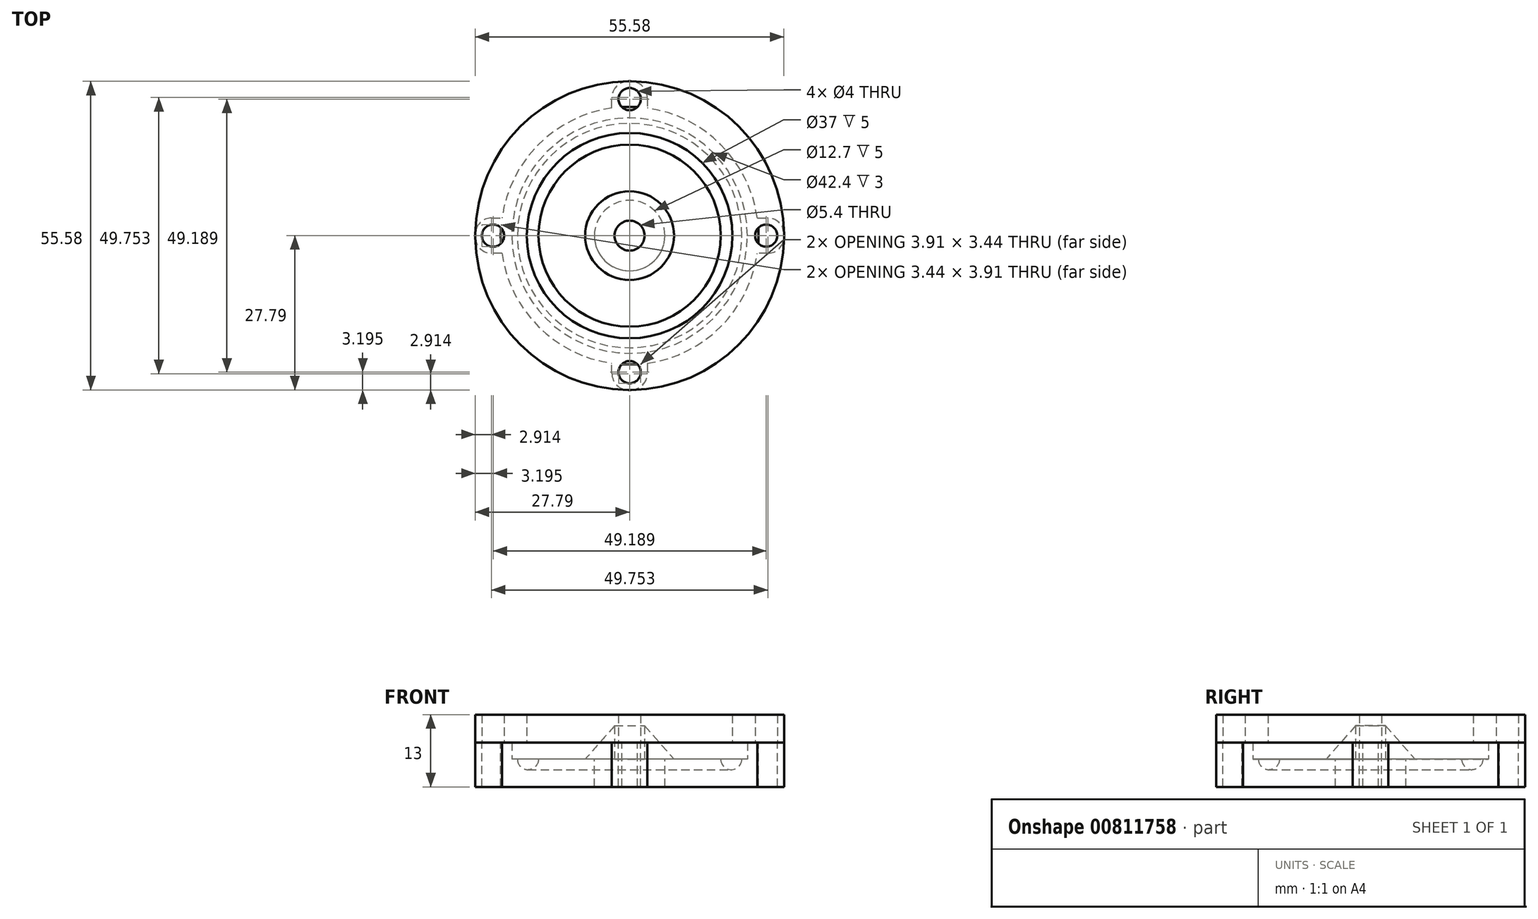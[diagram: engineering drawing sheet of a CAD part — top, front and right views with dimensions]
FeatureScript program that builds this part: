
annotation { "Feature Type Name" : "Feature", "Feature Type Description" : "" }
export const myFeature = defineFeature(function(context is Context, id is Id, definition is map)
    precondition{}
    {
        {
            assignVariable(context, id + "F0", {"name" : "thickness", "anyValue" : 5});
        }
        {
            var Q0;
            Q0=qCreatedBy(makeId("Top.planeOp"),FACE);
            var sketch = newSketch(context, id + "F1", { "sketchPlane" : qUnion([Q0])});
            skCircle(sketch, "E0", {"center": v(0, 0) * mm, "radius": 23.2 * mm});
            skCircle(sketch, "E1", {"center": v(0, 0) * mm, "radius": 21.2 * mm});
            skCircle(sketch, "E2", {"center": v(0, 0) * mm, "radius": 6.35 * mm});
            skSolve(sketch);
        }
        {
            var Q0;
            Q0=makeQuery(id+"F1.imprint","IMPRINT",FACE,{"disambiguationData":[TD([[makeQuery(id+"F1.imprint","IMPRINT",EDGE,{"derivedFrom":sQuery(id+"F1.wireOp",EDGE,"E1")}),1.0]])]});
            var Q1;
            Q1=makeQuery(id+"F1.imprint","IMPRINT",FACE,{"disambiguationData":[TD([[makeQuery(id+"F1.imprint","IMPRINT",EDGE,{"derivedFrom":sQuery(id+"F1.wireOp",EDGE,"E0")}),1.0]])]});
            extrude(context, id + "F2", {"entities" : qUnion([Q0, Q1]), "oppositeDirection" : true, "depth" : getVariable(context, 'thickness') * mm, "offsetDistance" : 25 * mm});
        }
        {
            var Q0;
            Q0=makeQuery(id+"F1.imprint","IMPRINT",FACE,{"disambiguationData":[TD([[makeQuery(id+"F1.imprint","IMPRINT",EDGE,{"derivedFrom":sQuery(id+"F1.wireOp",EDGE,"E0")}),1.0]])]});
            extrude(context, id + "F3", {"entities" : qUnion([Q0]), "operationType" : NewBodyOperationType.ADD, "depth" : 3 * mm, "offsetDistance" : 25 * mm});
        }
        {
            var Q0;
            Q0=qCreatedBy(makeId("Front.planeOp"),FACE);
            var sketch = newSketch(context, id + "F4", { "sketchPlane" : qUnion([Q0])});
            skLineSegment(sketch, "E3.0", {"start": v(-21.2, 0) * mm, "end": v(21.2, 0) * mm, "construction": true});
            skLineSegment(sketch, "E4", {"start": v(20.2, 0) * mm, "end": v(16.4, 0) * mm});
            skArc(sketch, "E5", {"start": v(16.4, 0) * mm, "mid": v(18.3, -1.9) * mm, "end": v(20.2, 0) * mm});
            skSolve(sketch);
        }
        {
            var Q0;
            Q0=makeQuery(id+"F4.imprint","IMPRINT",FACE,{"disambiguationData":[TD([[makeQuery(id+"F4.imprint","IMPRINT",EDGE,{"derivedFrom":sQuery(id+"F4.wireOp",EDGE,"E4")}),1.0]])]});
            var Q1;
            Q1=sQuery(id+"F1.wireOp",EDGE,"E1");
            revolve(context, id + "F5", {"operationType" : NewBodyOperationType.REMOVE, "surfaceOperationType" : NewSurfaceOperationType.NEW, "entities" : qUnion([Q0]), "axis" : qUnion([Q1]), "revolveType" : RevolveType.FULL, "oppositeDirection" : true});
        }
        {
            var Q0;
            Q0=makeQuery(id+"F3.opExtrude","CAP_FACE",FACE,{"disambiguationData":[OSD([sQuery(id+"F1.wireOp",EDGE,"E0"),sQuery(id+"F1.wireOp",EDGE,"E1")])],"isStart":false});
            var sketch = newSketch(context, id + "F6", { "sketchPlane" : qUnion([Q0])});
            skCircle(sketch, "E6.0", {"center": v(0, 0) * mm, "radius": 23.2 * mm, "construction": true});
            skLineSegment(sketch, "E7", {"start": v(-22.98, 3.2) * mm, "end": v(-24.8, 3.2) * mm});
            skLineSegment(sketch, "E8", {"start": v(-27.8, 0.2) * mm, "end": v(-27.8, -0.2) * mm});
            skLineSegment(sketch, "E9", {"start": v(-24.8, -3.2) * mm, "end": v(-22.98, -3.2) * mm});
            skLineSegment(sketch, "E10", {"start": v(0, 0) * mm, "end": v(-60.22, 0) * mm, "construction": true});
            skPoint(sketch, "E11", {"position": v(-27.8, 0) * mm});
            skCircle(sketch, "E12", {"center": v(-24.6, 0) * mm, "radius": 2 * mm});
            skPoint(sketch, "E13.visualSharp", {"position": v(-27.8, 3.2) * mm});
            skArc(sketch, "E13.filletArc", {"start": v(-24.8, 3.2) * mm, "mid": v(-26.92, 2.32) * mm, "end": v(-27.8, 0.2) * mm});
            skPoint(sketch, "E14.visualSharp", {"position": v(-27.8, -3.2) * mm});
            skArc(sketch, "E14.filletArc", {"start": v(-27.8, -0.2) * mm, "mid": v(-26.92, -2.32) * mm, "end": v(-24.8, -3.2) * mm});
            skPoint(sketch, "E15.1.0", {"position": v(3.2, -27.8) * mm});
            skPoint(sketch, "E15.1.1", {"position": v(0, -27.8) * mm});
            skArc(sketch, "E15.1.2", {"start": v(0.2, -27.8) * mm, "mid": v(2.32, -26.92) * mm, "end": v(3.2, -24.8) * mm});
            skLineSegment(sketch, "E15.1.3", {"start": v(-0.2, -27.8) * mm, "end": v(0.2, -27.8) * mm});
            skArc(sketch, "E15.1.4", {"start": v(-3.2, -24.8) * mm, "mid": v(-2.32, -26.92) * mm, "end": v(-0.2, -27.8) * mm});
            skPoint(sketch, "E15.1.5", {"position": v(-3.2, -27.8) * mm});
            skLineSegment(sketch, "E15.1.6", {"start": v(3.2, -24.8) * mm, "end": v(3.2, -22.98) * mm});
            skCircle(sketch, "E15.1.7", {"center": v(0, -24.6) * mm, "radius": 2 * mm});
            skLineSegment(sketch, "E15.1.8", {"start": v(-3.2, -22.98) * mm, "end": v(-3.2, -24.8) * mm});
            skPoint(sketch, "E15.2.0", {"position": v(27.8, 3.2) * mm});
            skPoint(sketch, "E15.2.1", {"position": v(27.8, 0) * mm});
            skArc(sketch, "E15.2.2", {"start": v(27.8, 0.2) * mm, "mid": v(26.92, 2.32) * mm, "end": v(24.8, 3.2) * mm});
            skLineSegment(sketch, "E15.2.3", {"start": v(27.8, -0.2) * mm, "end": v(27.8, 0.2) * mm});
            skArc(sketch, "E15.2.4", {"start": v(24.8, -3.2) * mm, "mid": v(26.92, -2.32) * mm, "end": v(27.8, -0.2) * mm});
            skPoint(sketch, "E15.2.5", {"position": v(27.8, -3.2) * mm});
            skLineSegment(sketch, "E15.2.6", {"start": v(24.8, 3.2) * mm, "end": v(22.98, 3.2) * mm});
            skCircle(sketch, "E15.2.7", {"center": v(24.6, 0) * mm, "radius": 2 * mm});
            skLineSegment(sketch, "E15.2.8", {"start": v(22.98, -3.2) * mm, "end": v(24.8, -3.2) * mm});
            skPoint(sketch, "E15.3.0", {"position": v(-3.2, 27.8) * mm});
            skPoint(sketch, "E15.3.1", {"position": v(0, 27.8) * mm});
            skArc(sketch, "E15.3.2", {"start": v(-0.2, 27.8) * mm, "mid": v(-2.32, 26.92) * mm, "end": v(-3.2, 24.8) * mm});
            skLineSegment(sketch, "E15.3.3", {"start": v(0.2, 27.8) * mm, "end": v(-0.2, 27.8) * mm});
            skArc(sketch, "E15.3.4", {"start": v(3.2, 24.8) * mm, "mid": v(2.32, 26.92) * mm, "end": v(0.2, 27.8) * mm});
            skPoint(sketch, "E15.3.5", {"position": v(3.2, 27.8) * mm});
            skLineSegment(sketch, "E15.3.6", {"start": v(-3.2, 24.8) * mm, "end": v(-3.2, 22.98) * mm});
            skCircle(sketch, "E15.3.7", {"center": v(0, 24.6) * mm, "radius": 2 * mm});
            skLineSegment(sketch, "E15.3.8", {"start": v(3.2, 22.98) * mm, "end": v(3.2, 24.8) * mm});
            skSolve(sketch);
        }
        {
            var Q0;
            {var subQ1=sQuery(id+"F6.wireOp",EDGE,"E7");Q0=makeQuery(id+"F6.imprint","IMPRINT",FACE,{"disambiguationData":[TD([[makeQuery(id+"F6.imprint","IMPRINT",EDGE,{"derivedFrom":subQ1}),1.0]])]});}
            var Q1;
            Q1=makeQuery(id+"F6.imprint","IMPRINT",FACE,{"disambiguationData":[TD([[makeQuery(id+"F6.imprint","IMPRINT",EDGE,{"derivedFrom":sQuery(id+"F6.wireOp",EDGE,"E15.3.2")}),1.0]])]});
            var Q2;
            Q2=makeQuery(id+"F6.imprint","IMPRINT",FACE,{"disambiguationData":[TD([[makeQuery(id+"F6.imprint","IMPRINT",EDGE,{"derivedFrom":sQuery(id+"F6.wireOp",EDGE,"E15.2.2")}),1.0]])]});
            var Q3;
            Q3=makeQuery(id+"F6.imprint","IMPRINT",FACE,{"disambiguationData":[TD([[makeQuery(id+"F6.imprint","IMPRINT",EDGE,{"derivedFrom":sQuery(id+"F6.wireOp",EDGE,"E15.1.2")}),1.0]])]});
            var Q4;
            Q4=makeQuery(id+"F2.opExtrude","CAP_FACE",FACE,{"disambiguationData":[OSD([sQuery(id+"F1.wireOp",EDGE,"E0")])],"isStart":false});
            extrude(context, id + "F7", {"entities" : qUnion([Q0, Q1, Q2, Q3]), "operationType" : NewBodyOperationType.ADD, "endBound" : BoundingType.UP_TO_SURFACE, "oppositeDirection" : true, "depth" : 25 * mm, "endBoundEntityFace" : qUnion([Q4]), "offsetDistance" : 25 * mm});
        }
        {
            var Q0;
            {var subQ0=sQuery(id+"F1.wireOp",EDGE,"E0");Q0=makeQuery(id+"F7.boolean.opBoolean","MERGE",FACE,{"derivedFrom":[makeQuery(id+"F3.opExtrude","CAP_FACE",FACE,{"disambiguationData":[OSD([subQ0,sQuery(id+"F1.wireOp",EDGE,"E1")])],"isStart":false}),makeQuery(id+"F7.opExtrude","CAP_FACE",FACE,{"disambiguationData":[OSD([subQ0,sQuery(id+"F6.wireOp",EDGE,"E7"),sQuery(id+"F6.wireOp",EDGE,"E8"),sQuery(id+"F6.wireOp",EDGE,"E9"),sQuery(id+"F6.wireOp",EDGE,"E12"),sQuery(id+"F6.wireOp",EDGE,"E13.filletArc"),sQuery(id+"F6.wireOp",EDGE,"E14.filletArc")])],"isStart":true}),makeQuery(id+"F7.opExtrude","CAP_FACE",FACE,{"disambiguationData":[OSD([subQ0,sQuery(id+"F6.wireOp",EDGE,"E15.1.2"),sQuery(id+"F6.wireOp",EDGE,"E15.1.3"),sQuery(id+"F6.wireOp",EDGE,"E15.1.4"),sQuery(id+"F6.wireOp",EDGE,"E15.1.6"),sQuery(id+"F6.wireOp",EDGE,"E15.1.7"),sQuery(id+"F6.wireOp",EDGE,"E15.1.8")])],"isStart":true}),makeQuery(id+"F7.opExtrude","CAP_FACE",FACE,{"disambiguationData":[OSD([subQ0,sQuery(id+"F6.wireOp",EDGE,"E15.2.2"),sQuery(id+"F6.wireOp",EDGE,"E15.2.3"),sQuery(id+"F6.wireOp",EDGE,"E15.2.4"),sQuery(id+"F6.wireOp",EDGE,"E15.2.6"),sQuery(id+"F6.wireOp",EDGE,"E15.2.7"),sQuery(id+"F6.wireOp",EDGE,"E15.2.8")])],"isStart":true}),makeQuery(id+"F7.opExtrude","CAP_FACE",FACE,{"disambiguationData":[OSD([subQ0,sQuery(id+"F6.wireOp",EDGE,"E15.3.2"),sQuery(id+"F6.wireOp",EDGE,"E15.3.3"),sQuery(id+"F6.wireOp",EDGE,"E15.3.4"),sQuery(id+"F6.wireOp",EDGE,"E15.3.6"),sQuery(id+"F6.wireOp",EDGE,"E15.3.7"),sQuery(id+"F6.wireOp",EDGE,"E15.3.8")])],"isStart":true})]});}
            var sketch = newSketch(context, id + "F8", { "sketchPlane" : qUnion([Q0])});
            skArc(sketch, "E16.0", {"start": v(-3.2, 22.98) * mm, "mid": v(-16.4, 16.4) * mm, "end": v(-22.98, 3.2) * mm});
            skArc(sketch, "E16.1", {"start": v(22.98, 3.2) * mm, "mid": v(16.4, 16.4) * mm, "end": v(3.2, 22.98) * mm});
            skArc(sketch, "E16.2", {"start": v(3.2, -22.98) * mm, "mid": v(16.4, -16.4) * mm, "end": v(22.98, -3.2) * mm});
            skArc(sketch, "E16.3", {"start": v(-22.98, -3.2) * mm, "mid": v(-16.4, -16.4) * mm, "end": v(-3.2, -22.98) * mm});
            skLineSegment(sketch, "E16.4", {"start": v(-24.8, -3.2) * mm, "end": v(-22.98, -3.2) * mm});
            skArc(sketch, "E16.5", {"start": v(-27.8, -0.2) * mm, "mid": v(-26.92, -2.32) * mm, "end": v(-24.8, -3.2) * mm});
            skLineSegment(sketch, "E16.6", {"start": v(-27.8, 0.2) * mm, "end": v(-27.8, -0.2) * mm});
            skArc(sketch, "E16.7", {"start": v(-24.8, 3.2) * mm, "mid": v(-26.92, 2.32) * mm, "end": v(-27.8, 0.2) * mm});
            skLineSegment(sketch, "E16.8", {"start": v(-22.98, 3.2) * mm, "end": v(-24.8, 3.2) * mm});
            skCircle(sketch, "E16.9", {"center": v(-24.6, 0) * mm, "radius": 2 * mm});
            skLineSegment(sketch, "E16.10", {"start": v(-3.2, 24.8) * mm, "end": v(-3.2, 22.98) * mm});
            skLineSegment(sketch, "E16.11", {"start": v(3.2, 22.98) * mm, "end": v(3.2, 24.8) * mm});
            skArc(sketch, "E16.12", {"start": v(3.2, 24.8) * mm, "mid": v(2.32, 26.92) * mm, "end": v(0.2, 27.8) * mm});
            skLineSegment(sketch, "E16.13", {"start": v(0.2, 27.8) * mm, "end": v(-0.2, 27.8) * mm});
            skArc(sketch, "E16.14", {"start": v(-0.2, 27.8) * mm, "mid": v(-2.32, 26.92) * mm, "end": v(-3.2, 24.8) * mm});
            skLineSegment(sketch, "E16.15", {"start": v(24.8, 3.2) * mm, "end": v(22.98, 3.2) * mm});
            skCircle(sketch, "E16.16", {"center": v(24.6, 0) * mm, "radius": 2 * mm});
            skArc(sketch, "E16.17", {"start": v(27.8, 0.2) * mm, "mid": v(26.92, 2.32) * mm, "end": v(24.8, 3.2) * mm});
            skLineSegment(sketch, "E16.18", {"start": v(22.98, -3.2) * mm, "end": v(24.8, -3.2) * mm});
            skArc(sketch, "E16.19", {"start": v(24.8, -3.2) * mm, "mid": v(26.92, -2.32) * mm, "end": v(27.8, -0.2) * mm});
            skLineSegment(sketch, "E16.20", {"start": v(27.8, -0.2) * mm, "end": v(27.8, 0.2) * mm});
            skCircle(sketch, "E16.21", {"center": v(0, -24.6) * mm, "radius": 2 * mm});
            skLineSegment(sketch, "E16.22", {"start": v(-3.2, -22.98) * mm, "end": v(-3.2, -24.8) * mm});
            skArc(sketch, "E16.23", {"start": v(-3.2, -24.8) * mm, "mid": v(-2.32, -26.92) * mm, "end": v(-0.2, -27.8) * mm});
            skLineSegment(sketch, "E16.24", {"start": v(3.2, -24.8) * mm, "end": v(3.2, -22.98) * mm});
            skArc(sketch, "E16.25", {"start": v(0.2, -27.8) * mm, "mid": v(2.32, -26.92) * mm, "end": v(3.2, -24.8) * mm});
            skLineSegment(sketch, "E16.26", {"start": v(-0.2, -27.8) * mm, "end": v(0.2, -27.8) * mm});
            skCircle(sketch, "E17.0", {"center": v(0, 0) * mm, "radius": 21.2 * mm, "construction": true});
            skCircle(sketch, "E18", {"center": v(0, 0) * mm, "radius": 18.5 * mm});
            skCircle(sketch, "E19.0", {"center": v(0, 24.6) * mm, "radius": 2 * mm});
            skCircle(sketch, "E20", {"center": v(0, 0) * mm, "radius": 27.8 * mm});
            skSolve(sketch);
        }
        {
            var Q0;
            Q0=makeQuery(id+"F8.imprint","IMPRINT",FACE,{"disambiguationData":[TD([[makeQuery(id+"F8.imprint","IMPRINT",EDGE,{"derivedFrom":sQuery(id+"F8.wireOp",EDGE,"E16.0")}),1.0]])]});
            var Q1;
            Q1=makeQuery(id+"F8.imprint","IMPRINT",FACE,{"disambiguationData":[TD([[makeQuery(id+"F8.imprint","IMPRINT",EDGE,{"derivedFrom":sQuery(id+"F8.wireOp",EDGE,"E18")}),-1.0]])]});
            var Q2;
            Q2=makeQuery(id+"F8.imprint","IMPRINT",FACE,{"disambiguationData":[TD([[makeQuery(id+"F8.imprint","IMPRINT",EDGE,{"derivedFrom":sQuery(id+"F8.wireOp",EDGE,"E16.1")}),-1.0]])]});
            var Q3;
            Q3=makeQuery(id+"F8.imprint","IMPRINT",FACE,{"disambiguationData":[TD([[makeQuery(id+"F8.imprint","IMPRINT",EDGE,{"derivedFrom":sQuery(id+"F8.wireOp",EDGE,"E16.3")}),-1.0]])]});
            var Q4;
            Q4=makeQuery(id+"F8.imprint","IMPRINT",FACE,{"disambiguationData":[TD([[makeQuery(id+"F8.imprint","IMPRINT",EDGE,{"derivedFrom":sQuery(id+"F8.wireOp",EDGE,"E16.0")}),-1.0]])]});
            var Q5;
            Q5=makeQuery(id+"F8.imprint","IMPRINT",FACE,{"disambiguationData":[TD([[makeQuery(id+"F8.imprint","IMPRINT",EDGE,{"derivedFrom":sQuery(id+"F8.wireOp",EDGE,"E16.2")}),-1.0]])]});
            extrude(context, id + "F9", {"entities" : qUnion([Q0, Q1, Q2, Q3, Q4, Q5]), "depth" : 5 * mm, "offsetDistance" : 25 * mm});
        }
        {
            var Q0;
            Q0=qCreatedBy(makeId("Front.planeOp"),FACE);
            var sketch = newSketch(context, id + "F10", { "sketchPlane" : qUnion([Q0])});
            skLineSegment(sketch, "E21.0", {"start": v(-6.35, 0) * mm, "end": v(6.35, 0) * mm, "construction": true});
            skLineSegment(sketch, "E22", {"start": v(8, 0) * mm, "end": v(2.7, 6) * mm});
            skLineSegment(sketch, "E23", {"start": v(2.7, 6) * mm, "end": v(2.7, 0) * mm});
            skLineSegment(sketch, "E24", {"start": v(2.7, 0) * mm, "end": v(8, 0) * mm});
            skLineSegment(sketch, "E25", {"start": v(0, 0) * mm, "end": v(0, 10.37) * mm, "construction": true});
            skSolve(sketch);
        }
        {
            var Q0;
            Q0=makeQuery(id+"F10.imprint","IMPRINT",FACE,{"disambiguationData":[TD([[makeQuery(id+"F10.imprint","IMPRINT",EDGE,{"derivedFrom":sQuery(id+"F10.wireOp",EDGE,"E22")}),1.0]])]});
            var Q1;
            Q1=sQuery(id+"F10.wireOp",EDGE,"E25");
            revolve(context, id + "F11", {"operationType" : NewBodyOperationType.ADD, "surfaceOperationType" : NewSurfaceOperationType.NEW, "entities" : qUnion([Q0]), "axis" : qUnion([Q1]), "revolveType" : RevolveType.FULL});
        }
    });
